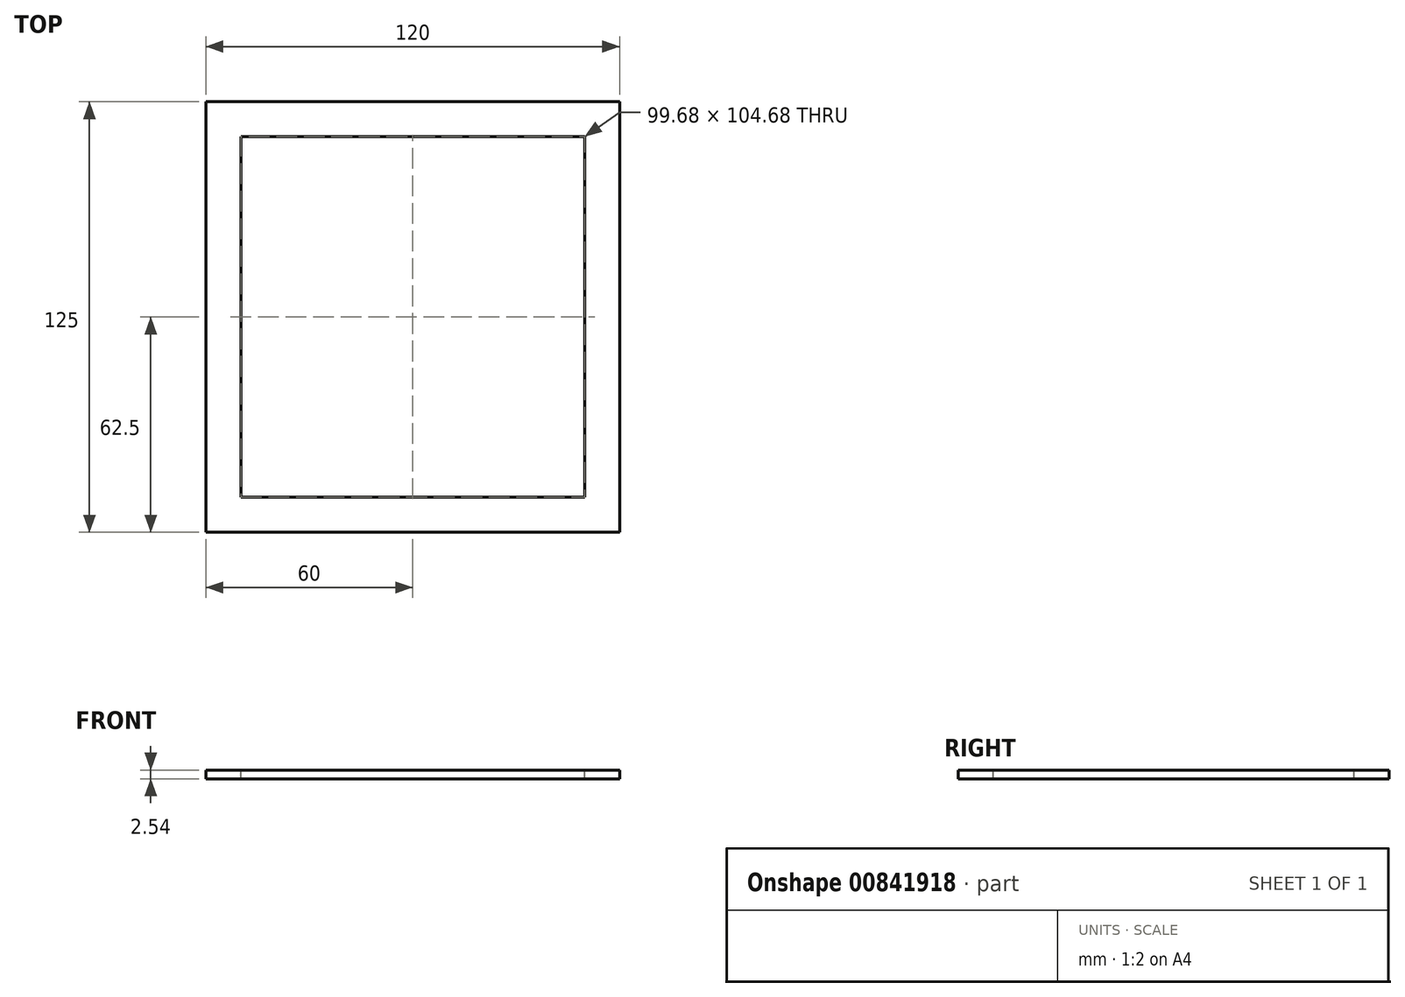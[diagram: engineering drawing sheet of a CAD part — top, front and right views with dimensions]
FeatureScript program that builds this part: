
annotation { "Feature Type Name" : "Feature", "Feature Type Description" : "" }
export const myFeature = defineFeature(function(context is Context, id is Id, definition is map)
    precondition{}
    {
        {
            var Q0;
            Q0=qCreatedBy(makeId("Top.planeOp"),FACE);
            var sketch = newSketch(context, id + "F0", { "sketchPlane" : qUnion([Q0])});
            skLineSegment(sketch, "E0.bottom", {"start": v(-57.15, -74.2) * mm, "end": v(62.85, -74.2) * mm});
            skLineSegment(sketch, "E0.top", {"start": v(-57.15, 50.8) * mm, "end": v(62.85, 50.8) * mm});
            skLineSegment(sketch, "E0.left", {"start": v(-57.15, -74.2) * mm, "end": v(-57.15, 50.8) * mm});
            skLineSegment(sketch, "E0.right", {"start": v(62.85, -74.2) * mm, "end": v(62.85, 50.8) * mm});
            skLineSegment(sketch, "E1.bottom", {"start": v(52.7, -64.04) * mm, "end": v(-46.99, -64.04) * mm});
            skLineSegment(sketch, "E1.top", {"start": v(52.69, 40.64) * mm, "end": v(-47, 40.64) * mm});
            skLineSegment(sketch, "E1.left", {"start": v(52.7, -64.04) * mm, "end": v(52.69, 40.64) * mm});
            skLineSegment(sketch, "E1.right", {"start": v(-46.99, -64.04) * mm, "end": v(-47, 40.64) * mm});
            skSolve(sketch);
        }
        {
            var Q0;
            Q0 = qSketchRegion(id + "F0", true);
            extrude(context, id + "F1", {"entities" : qUnion([Q0]), "oppositeDirection" : true, "depth" : 2.54 * mm, "offsetDistance" : 25.4 * mm});
        }
    });
